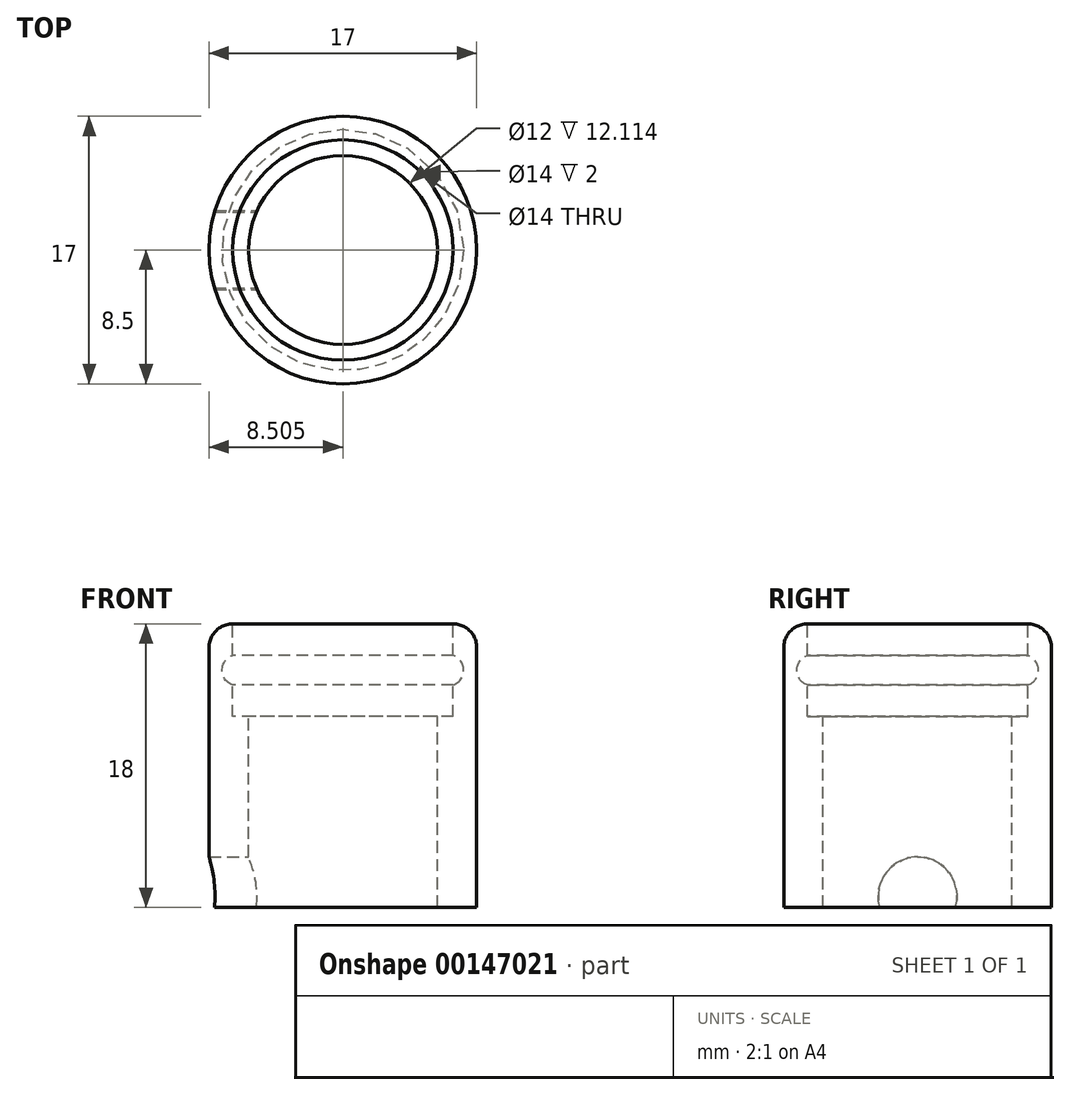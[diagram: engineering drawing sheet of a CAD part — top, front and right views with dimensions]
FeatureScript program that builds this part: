
annotation { "Feature Type Name" : "Feature", "Feature Type Description" : "" }
export const myFeature = defineFeature(function(context is Context, id is Id, definition is map)
    precondition{}
    {
        {
            var Q0;
            Q0=qCreatedBy(makeId("Front.planeOp"),FACE);
            var sketch = newSketch(context, id + "F0", { "sketchPlane" : qUnion([Q0])});
            skLineSegment(sketch, "E0", {"start": v(-30.75, 12.65) * mm, "end": v(-30.75, -5.35) * mm});
            skLineSegment(sketch, "E1", {"start": v(-28.25, -5.35) * mm, "end": v(-30.75, -5.35) * mm});
            skLineSegment(sketch, "E2", {"start": v(-28.25, -5.35) * mm, "end": v(-28.25, 6.77) * mm});
            skLineSegment(sketch, "E3", {"start": v(-28.25, 6.77) * mm, "end": v(-29.25, 6.77) * mm});
            skLineSegment(sketch, "E4", {"start": v(-29.25, 6.77) * mm, "end": v(-29.25, 8.77) * mm});
            skArc(sketch, "E5", {"start": v(-29.25, 10.65) * mm, "mid": v(-29.91, 9.71) * mm, "end": v(-29.25, 8.77) * mm});
            skLineSegment(sketch, "E6", {"start": v(-29.25, 10.65) * mm, "end": v(-29.25, 12.65) * mm});
            skLineSegment(sketch, "E7", {"start": v(-29.25, 12.65) * mm, "end": v(-30.75, 12.65) * mm});
            skLineSegment(sketch, "E8", {"start": v(-22.25, 18.97) * mm, "end": v(-22.25, -12.42) * mm});
            skPoint(sketch, "E9", {"position": v(-30.75, -3.71) * mm});
            skSolve(sketch);
        }
        {
            var Q0;
            Q0=makeQuery(id+"F0.imprint","IMPRINT",FACE,{"disambiguationData":[TD([[makeQuery(id+"F0.imprint","IMPRINT",EDGE,{"derivedFrom":sQuery(id+"F0.wireOp",EDGE,"E0")}),1.0]])]});
            var Q1;
            Q1=sQuery(id+"F0.wireOp",EDGE,"E8");
            revolve(context, id + "F1", {"entities" : qUnion([Q0]), "axis" : qUnion([Q1]), "revolveType" : RevolveType.FULL});
        }
        {
            var Q0;
            Q0=makeQuery(id+"F1.opRevolve","SWEPT_EDGE",EDGE,{"disambiguationData":[OSD([sQuery(id+"F0.wireOp",EDGE,"E0"),sQuery(id+"F0.wireOp",EDGE,"E7")])]});
            fillet(context, id + "F2", {"entities" : qUnion([Q0]), "radius" : 1.5 * mm, "tangentPropagation" : true, "allowEdgeOverflow" : false});
        }
        {
            var Q0;
            Q0=qCreatedBy(makeId("Right.planeOp"),FACE);
            cPlane(context, id + "F3", {"entities" : qUnion([Q0]), "cplaneType" : CPlaneType.OFFSET, "offset" : 25 * mm, "oppositeDirection" : true, "width" : 150 * mm, "height" : 150 * mm});
        }
        {
            var Q0;
            Q0=qCreatedBy(id+"F3.planeOp",FACE);
            var sketch = newSketch(context, id + "F4", { "sketchPlane" : qUnion([Q0])});
            skCircle(sketch, "E10", {"center": v(0, -4.65) * mm, "radius": 2.5 * mm});
            skSolve(sketch);
        }
        {
            var Q0;
            Q0=makeQuery(id+"F4.imprint","IMPRINT",FACE,{"disambiguationData":[TD([[makeQuery(id+"F4.imprint","IMPRINT",EDGE,{"derivedFrom":sQuery(id+"F4.wireOp",EDGE,"E10")}),1.0]])]});
            extrude(context, id + "F5", {"entities" : qUnion([Q0]), "operationType" : NewBodyOperationType.REMOVE, "oppositeDirection" : true, "depth" : 25 * mm, "offsetDistance" : 25 * mm});
        }
    });
